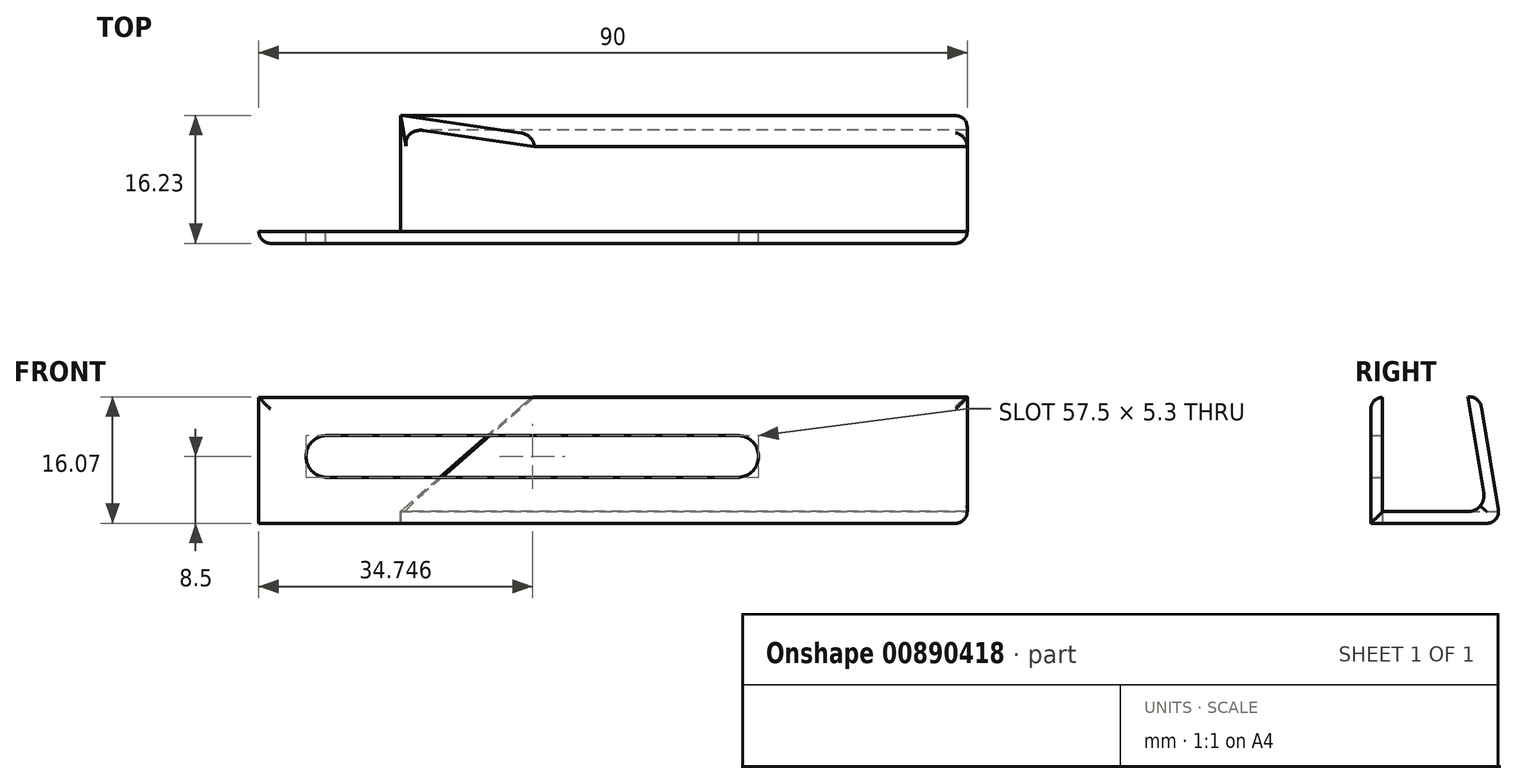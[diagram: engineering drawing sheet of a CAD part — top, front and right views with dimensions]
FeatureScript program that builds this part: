
annotation { "Feature Type Name" : "Feature", "Feature Type Description" : "" }
export const myFeature = defineFeature(function(context is Context, id is Id, definition is map)
    precondition{}
    {
        {
            var Q0;
            Q0=qCreatedBy(makeId("Top.planeOp"),FACE);
            var sketch = newSketch(context, id + "F0", { "sketchPlane" : qUnion([Q0])});
            skLineSegment(sketch, "E0", {"start": v(-34.47, 0) * mm, "end": v(37.53, 0) * mm});
            skLineSegment(sketch, "E1", {"start": v(37.53, 0) * mm, "end": v(37.53, 15) * mm});
            skLineSegment(sketch, "E2", {"start": v(37.53, 15) * mm, "end": v(-34.47, 15) * mm});
            skLineSegment(sketch, "E3", {"start": v(-34.47, 15) * mm, "end": v(-34.47, 0) * mm});
            skSolve(sketch);
        }
        {
            var Q0;
            Q0=makeQuery(id+"F0.imprint","IMPRINT",FACE,{"disambiguationData":[TD([[makeQuery(id+"F0.imprint","IMPRINT",EDGE,{"derivedFrom":sQuery(id+"F0.wireOp",EDGE,"E0")}),1.0]])]});
            extrude(context, id + "F1", {"entities" : qUnion([Q0]), "depth" : 1.5 * mm, "offsetDistance" : 25 * mm});
        }
        {
            var Q0;
            Q0=makeQuery(id+"F1.opExtrude","SWEPT_FACE",FACE,{"disambiguationData":[OSD([sQuery(id+"F0.wireOp",EDGE,"E0")])]});
            var sketch = newSketch(context, id + "F2", { "sketchPlane" : qUnion([Q0])});
            skLineSegment(sketch, "E4", {"start": v(37.53, 0) * mm, "end": v(37.53, 16) * mm});
            skLineSegment(sketch, "E5", {"start": v(37.53, 16) * mm, "end": v(-52.47, 16) * mm});
            skLineSegment(sketch, "E6", {"start": v(-52.47, 16) * mm, "end": v(-52.47, 0) * mm});
            skLineSegment(sketch, "E7", {"start": v(-52.47, 0) * mm, "end": v(37.53, 0) * mm});
            skLineSegment(sketch, "E8", {"start": v(-46.47, 8.5) * mm, "end": v(8.53, 8.5) * mm, "construction": true});
            skLineSegment(sketch, "E9", {"start": v(-43.97, 11.15) * mm, "end": v(-43.97, 5.85) * mm});
            skLineSegment(sketch, "E10", {"start": v(-43.97, 5.85) * mm, "end": v(8.53, 5.85) * mm});
            skLineSegment(sketch, "E11", {"start": v(8.53, 5.85) * mm, "end": v(8.53, 11.15) * mm});
            skLineSegment(sketch, "E12", {"start": v(8.53, 11.15) * mm, "end": v(-43.97, 11.15) * mm});
            skArc(sketch, "E13", {"start": v(-43.97, 11.15) * mm, "mid": v(-46.47, 8.5) * mm, "end": v(-43.97, 5.85) * mm});
            skLineSegment(sketch, "E14", {"start": v(8.53, 8.5) * mm, "end": v(11.03, 8.5) * mm, "construction": true});
            skArc(sketch, "E15", {"start": v(8.53, 5.85) * mm, "mid": v(11.03, 8.5) * mm, "end": v(8.53, 11.15) * mm});
            skSolve(sketch);
        }
        {
            var Q0;
            {var subQ3=sQuery(id+"F0.wireOp",EDGE,"E0");var subQ4=makeQuery(id+"F1.opExtrude","CAP_EDGE",EDGE,{"disambiguationData":[OSD([subQ3])],"isStart":false});Q0=makeQuery(id+"F2.imprint","IMPRINT",FACE,{"disambiguationData":[TD([[makeQuery(id+"F2.imprint","IMPRINT",EDGE,{"derivedFrom":subQ4}),-1.0]])]});}
            var Q1;
            {var subQ1=sQuery(id+"F2.wireOp",EDGE,"E5");Q1=makeQuery(id+"F2.imprint","IMPRINT",FACE,{"disambiguationData":[TD([[makeQuery(id+"F2.imprint","IMPRINT",EDGE,{"derivedFrom":subQ1}),1.0]])]});}
            extrude(context, id + "F3", {"entities" : qUnion([Q0, Q1]), "operationType" : NewBodyOperationType.ADD, "depth" : 1.5 * mm, "offsetDistance" : 25 * mm});
        }
        {
            var Q0;
            Q0=makeQuery(id+"F1.opExtrude","CAP_EDGE",EDGE,{"disambiguationData":[OSD([sQuery(id+"F0.wireOp",EDGE,"E2")])],"isStart":false});
            chamfer(context, id + "F4", {"entities" : qUnion([Q0]), "chamferType" : ChamferType.TWO_OFFSETS, "width1" : 0.25 * mm, "oppositeDirection" : false, "width2" : 1.5 * mm, "tangentPropagation" : true});
        }
        {
            var Q0;
            Q0=makeQuery(id+"F4.opChamfer","BLEND_FACE",FACE,{"disambiguationData":[OSD([sQuery(id+"F0.wireOp",EDGE,"E2")])]});
            var sketch = newSketch(context, id + "F5", { "sketchPlane" : qUnion([Q0])});
            skLineSegment(sketch, "E16", {"start": v(-37.53, -0.95) * mm, "end": v(-37.53, 14.05) * mm});
            skLineSegment(sketch, "E17", {"start": v(34.47, -0.95) * mm, "end": v(-37.53, -0.95) * mm});
            skLineSegment(sketch, "E18", {"start": v(17.47, 14.05) * mm, "end": v(34.47, -0.95) * mm});
            skLineSegment(sketch, "E19", {"start": v(17.47, 14.05) * mm, "end": v(-37.53, 14.05) * mm});
            skSolve(sketch);
        }
        {
            var Q0;
            Q0=makeQuery(id+"F5.imprint","IMPRINT",FACE,{"disambiguationData":[TD([[makeQuery(id+"F5.imprint","IMPRINT",EDGE,{"derivedFrom":sQuery(id+"F5.wireOp",EDGE,"E16")}),-1.0]])]});
            extrude(context, id + "F6", {"entities" : qUnion([Q0]), "operationType" : NewBodyOperationType.ADD, "oppositeDirection" : true, "depth" : 1.5 * mm, "offsetDistance" : 25 * mm});
        }
        {
            var Q0;
            Q0=makeQuery(id+"F6.boolean.opBoolean","MERGE",EDGE,{"derivedFrom":[makeQuery(id+"F4.opChamfer","BLEND_EDGE",EDGE,{"blendedFrom":[makeQuery(id+"F1.opExtrude","CAP_EDGE",EDGE,{"disambiguationData":[OSD([sQuery(id+"F0.wireOp",EDGE,"E2")])],"isStart":false}),makeQuery(id+"F3.boolean.opBoolean","MERGE",FACE,{"derivedFrom":[makeQuery(id+"F1.opExtrude","SWEPT_FACE",FACE,{"disambiguationData":[OSD([sQuery(id+"F0.wireOp",EDGE,"E1")])]}),makeQuery(id+"F3.opExtrude","SWEPT_FACE",FACE,{"disambiguationData":[OSD([sQuery(id+"F2.wireOp",EDGE,"E4")])]})]})],"blendedInto":[makeQuery(id+"F3.boolean.opBoolean","MERGE",FACE,{"derivedFrom":[makeQuery(id+"F1.opExtrude","SWEPT_FACE",FACE,{"disambiguationData":[OSD([sQuery(id+"F0.wireOp",EDGE,"E1")])]}),makeQuery(id+"F3.opExtrude","SWEPT_FACE",FACE,{"disambiguationData":[OSD([sQuery(id+"F2.wireOp",EDGE,"E4")])]})]})]}),makeQuery(id+"F6.opExtrude","CAP_EDGE",EDGE,{"disambiguationData":[OSD([sQuery(id+"F5.wireOp",EDGE,"E16")])],"isStart":true})]});
            var Q1;
            Q1=makeQuery(id+"F3.boolean.opBoolean","MERGE",EDGE,{"derivedFrom":[makeQuery(id+"F1.opExtrude","CAP_EDGE",EDGE,{"disambiguationData":[OSD([sQuery(id+"F0.wireOp",EDGE,"E1")])],"isStart":true}),makeQuery(id+"F3.opExtrude","SWEPT_EDGE",EDGE,{"disambiguationData":[OSD([sQuery(id+"F2.wireOp",EDGE,"E4"),sQuery(id+"F2.wireOp",EDGE,"E7")])]})]});
            var Q2;
            Q2=makeQuery(id+"F3.opExtrude","CAP_EDGE",EDGE,{"disambiguationData":[OSD([sQuery(id+"F2.wireOp",EDGE,"E4")])],"isStart":false});
            var Q3;
            Q3=makeQuery(id+"F3.opExtrude","CAP_EDGE",EDGE,{"disambiguationData":[OSD([sQuery(id+"F2.wireOp",EDGE,"E5")])],"isStart":false});
            var Q4;
            Q4=makeQuery(id+"F3.opExtrude","CAP_EDGE",EDGE,{"disambiguationData":[OSD([sQuery(id+"F2.wireOp",EDGE,"E6")])],"isStart":false});
            var Q5;
            Q5=makeQuery(id+"F6.opExtrude","CAP_EDGE",EDGE,{"disambiguationData":[OSD([sQuery(id+"F5.wireOp",EDGE,"E19")])],"isStart":true});
            var Q6;
            {var subQ0=sQuery(id+"F0.wireOp",EDGE,"E2");Q6=makeQuery(id+"F4.opChamfer","BLEND_EDGE",EDGE,{"blendedFrom":[makeQuery(id+"F1.opExtrude","CAP_EDGE",EDGE,{"disambiguationData":[OSD([subQ0])],"isStart":false}),makeQuery(id+"F3.boolean.opBoolean","MERGE",FACE,{"derivedFrom":[makeQuery(id+"F1.opExtrude","CAP_FACE",FACE,{"disambiguationData":[OSD([sQuery(id+"F0.wireOp",EDGE,"E0"),sQuery(id+"F0.wireOp",EDGE,"E1"),subQ0,sQuery(id+"F0.wireOp",EDGE,"E3")])],"isStart":true}),makeQuery(id+"F3.opExtrude","SWEPT_FACE",FACE,{"disambiguationData":[OSD([sQuery(id+"F2.wireOp",EDGE,"E7")])]})]})],"blendedInto":[makeQuery(id+"F3.boolean.opBoolean","MERGE",FACE,{"derivedFrom":[makeQuery(id+"F1.opExtrude","CAP_FACE",FACE,{"disambiguationData":[OSD([sQuery(id+"F0.wireOp",EDGE,"E0"),sQuery(id+"F0.wireOp",EDGE,"E1"),subQ0,sQuery(id+"F0.wireOp",EDGE,"E3")])],"isStart":true}),makeQuery(id+"F3.opExtrude","SWEPT_FACE",FACE,{"disambiguationData":[OSD([sQuery(id+"F2.wireOp",EDGE,"E7")])]})]})]});}
            fillet(context, id + "F7", {"entities" : qUnion([Q0, Q1, Q2, Q3, Q4, Q5, Q6]), "radius" : 1.5 * mm, "tangentPropagation" : true, "allowEdgeOverflow" : false});
        }
        {
            var Q0;
            Q0=makeQuery(id+"F6.boolean.opBoolean","INTERSECT",EDGE,{"derivedFrom":[makeQuery(id+"F1.opExtrude","CAP_FACE",FACE,{"disambiguationData":[OSD([sQuery(id+"F0.wireOp",EDGE,"E0"),sQuery(id+"F0.wireOp",EDGE,"E1"),sQuery(id+"F0.wireOp",EDGE,"E2"),sQuery(id+"F0.wireOp",EDGE,"E3")])],"isStart":false}),makeQuery(id+"F6.opExtrude","CAP_FACE",FACE,{"disambiguationData":[OSD([sQuery(id+"F5.wireOp",EDGE,"E16"),sQuery(id+"F5.wireOp",EDGE,"E17"),sQuery(id+"F5.wireOp",EDGE,"E18"),sQuery(id+"F5.wireOp",EDGE,"E19")])],"isStart":false})]});
            var Q1;
            Q1=makeQuery(id+"F1.opExtrude","CAP_EDGE",EDGE,{"disambiguationData":[OSD([sQuery(id+"F0.wireOp",EDGE,"E0")])],"isStart":false});
            fillet(context, id + "F8", {"entities" : qUnion([Q0, Q1]), "radius" : 2 * mm, "tangentPropagation" : true, "allowEdgeOverflow" : false});
        }
    });
